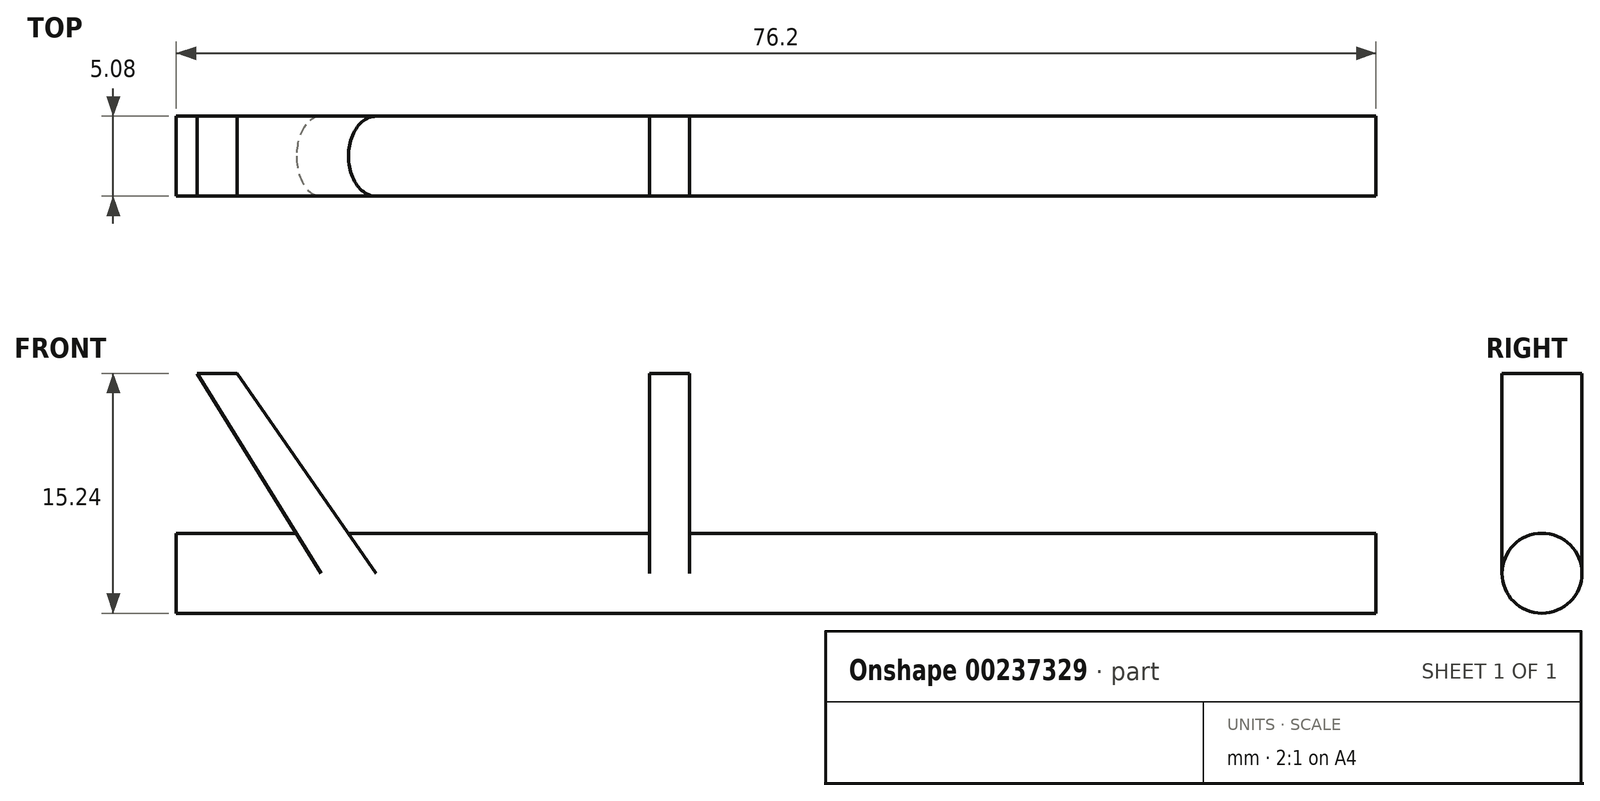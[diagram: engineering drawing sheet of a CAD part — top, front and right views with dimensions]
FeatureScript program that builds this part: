
annotation { "Feature Type Name" : "Feature", "Feature Type Description" : "" }
export const myFeature = defineFeature(function(context is Context, id is Id, definition is map)
    precondition{}
    {
        {
            var Q0;
            Q0=qCreatedBy(makeId("Front.planeOp"),FACE);
            var sketch = newSketch(context, id + "F0", { "sketchPlane" : qUnion([Q0])});
            skLineSegment(sketch, "E0", {"start": v(0, 0) * mm, "end": v(63.5, 0) * mm});
            skLineSegment(sketch, "E1", {"start": v(63.5, 0) * mm, "end": v(63.5, 2.54) * mm});
            skLineSegment(sketch, "E2", {"start": v(63.5, 2.54) * mm, "end": v(0, 2.54) * mm});
            skLineSegment(sketch, "E3", {"start": v(0, 2.54) * mm, "end": v(0, 0) * mm});
            skLineSegment(sketch, "E4", {"start": v(0, 0) * mm, "end": v(-12.7, 0) * mm});
            skLineSegment(sketch, "E5", {"start": v(-12.7, 0) * mm, "end": v(-12.7, 2.54) * mm});
            skLineSegment(sketch, "E6", {"start": v(-12.7, 2.54) * mm, "end": v(0, 2.54) * mm});
            skSolve(sketch);
        }
        {
            var Q0;
            Q0=qCreatedBy(makeId("Front.planeOp"),FACE);
            var sketch = newSketch(context, id + "F1", { "sketchPlane" : qUnion([Q0])});
            skLineSegment(sketch, "E7", {"start": v(17.37, 0) * mm, "end": v(17.37, 12.7) * mm});
            skLineSegment(sketch, "E8", {"start": v(17.37, 12.7) * mm, "end": v(19.91, 12.7) * mm});
            skLineSegment(sketch, "E9", {"start": v(19.91, 12.7) * mm, "end": v(19.91, 0) * mm});
            skLineSegment(sketch, "E10", {"start": v(19.91, 0) * mm, "end": v(17.37, 0) * mm});
            skLineSegment(sketch, "E11", {"start": v(0, 0) * mm, "end": v(-8.83, 12.7) * mm});
            skLineSegment(sketch, "E12", {"start": v(-8.83, 12.7) * mm, "end": v(-11.37, 12.7) * mm});
            skLineSegment(sketch, "E13", {"start": v(-11.37, 12.7) * mm, "end": v(-3.5, 0) * mm});
            skLineSegment(sketch, "E14", {"start": v(-3.5, 0) * mm, "end": v(0, 0) * mm});
            skSolve(sketch);
        }
        {
            var Q0;
            Q0=makeQuery(id+"F1.imprint","IMPRINT",FACE,{"disambiguationData":[TD([[makeQuery(id+"F1.imprint","IMPRINT",EDGE,{"derivedFrom":sQuery(id+"F1.wireOp",EDGE,"E11")}),1.0]])]});
            var Q1;
            Q1=makeQuery(id+"F1.imprint","IMPRINT",FACE,{"disambiguationData":[TD([[makeQuery(id+"F1.imprint","IMPRINT",EDGE,{"derivedFrom":sQuery(id+"F1.wireOp",EDGE,"E7")}),-1.0]])]});
            extrude(context, id + "F2", {"entities" : qUnion([Q0, Q1]), "depth" : 5.08 * mm, "symmetric" : true});
        }
        {
            var Q0;
            Q0=makeQuery(id+"F0.imprint","IMPRINT",FACE,{"disambiguationData":[TD([[makeQuery(id+"F0.imprint","IMPRINT",EDGE,{"derivedFrom":sQuery(id+"F0.wireOp",EDGE,"E0")}),1.0]])]});
            var Q1;
            Q1=makeQuery(id+"F0.imprint","IMPRINT",FACE,{"disambiguationData":[TD([[makeQuery(id+"F0.imprint","IMPRINT",EDGE,{"derivedFrom":sQuery(id+"F0.wireOp",EDGE,"E3")}),-1.0]])]});
            var Q2;
            Q2=sQuery(id+"F0.wireOp",EDGE,"E0");
            revolve(context, id + "F3", {"operationType" : NewBodyOperationType.ADD, "entities" : qUnion([Q0, Q1]), "axis" : qUnion([Q2]), "revolveType" : RevolveType.FULL});
        }
    });
